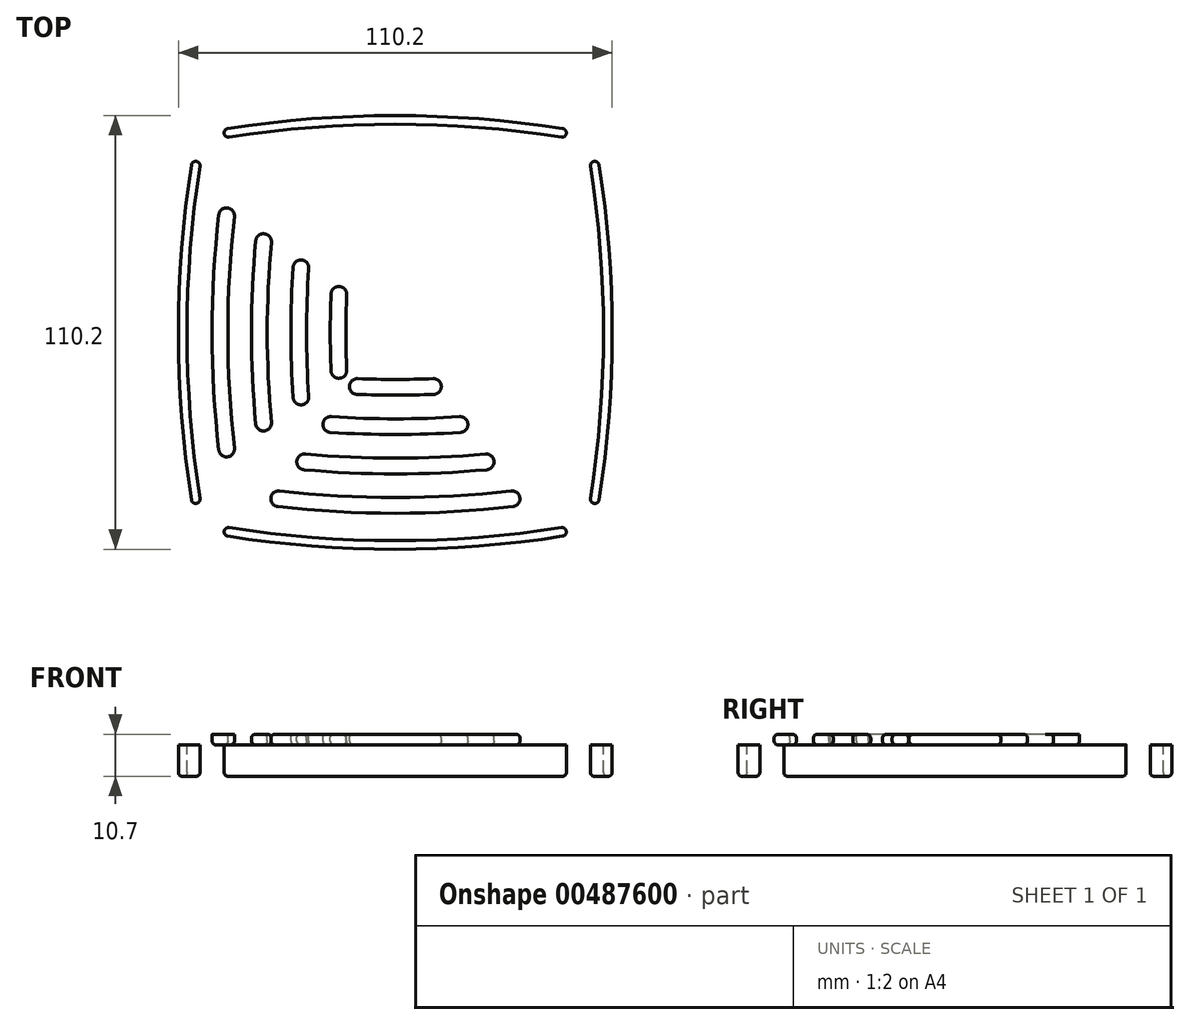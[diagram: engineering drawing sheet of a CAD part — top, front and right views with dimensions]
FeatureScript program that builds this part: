
annotation { "Feature Type Name" : "Feature", "Feature Type Description" : "" }
export const myFeature = defineFeature(function(context is Context, id is Id, definition is map)
    precondition{}
    {
        {
            var Q0;
            Q0=qCreatedBy(makeId("Top.planeOp"),FACE);
            var sketch = newSketch(context, id + "F0", { "sketchPlane" : qUnion([Q0])});
            skArc(sketch, "E0", {"start": v(58, 58) * mm, "mid": v(0, 64) * mm, "end": v(-58, 58) * mm});
            skPoint(sketch, "E1", {"position": v(0, 64) * mm});
            skArc(sketch, "E2.MirrorCS", {"start": v(58, -58) * mm, "mid": v(0, -64) * mm, "end": v(-58, -58) * mm});
            skArc(sketch, "E3", {"start": v(-58, 58) * mm, "mid": v(-64, 0) * mm, "end": v(-58, -58) * mm});
            skArc(sketch, "E4.MirrorCS", {"start": v(58, 58) * mm, "mid": v(64, 0) * mm, "end": v(58, -58) * mm});
            skSolve(sketch);
        }
        {
            var Q0;
            Q0=makeQuery(id+"F0.imprint","IMPRINT",FACE,{"disambiguationData":[TD([[makeQuery(id+"F0.imprint","IMPRINT",EDGE,{"derivedFrom":sQuery(id+"F0.wireOp",EDGE,"E0")}),1.0]])]});
            extrude(context, id + "F1", {"entities" : qUnion([Q0]), "depth" : 2.7 * mm});
        }
        {
            var Q0;
            Q0=makeQuery(id+"F1.opExtrude","SWEPT_EDGE",EDGE,{"disambiguationData":[OSD([sQuery(id+"F0.wireOp",EDGE,"E0"),sQuery(id+"F0.wireOp",EDGE,"E3")])]});
            var Q1;
            Q1=makeQuery(id+"F1.opExtrude","SWEPT_EDGE",EDGE,{"disambiguationData":[OSD([sQuery(id+"F0.wireOp",EDGE,"E2.MirrorCS"),sQuery(id+"F0.wireOp",EDGE,"E3")])]});
            var Q2;
            Q2=makeQuery(id+"F1.opExtrude","SWEPT_EDGE",EDGE,{"disambiguationData":[OSD([sQuery(id+"F0.wireOp",EDGE,"E0"),sQuery(id+"F0.wireOp",EDGE,"E4.MirrorCS")])]});
            var Q3;
            Q3=makeQuery(id+"F1.opExtrude","SWEPT_EDGE",EDGE,{"disambiguationData":[OSD([sQuery(id+"F0.wireOp",EDGE,"E2.MirrorCS"),sQuery(id+"F0.wireOp",EDGE,"E4.MirrorCS")])]});
            fillet(context, id + "F2", {"entities" : qUnion([Q0, Q1, Q2, Q3]), "radius" : 20 * mm, "tangentPropagation" : true, "allowEdgeOverflow" : false});
        }
        {
            var Q0;
            Q0=makeQuery(id+"F1.opExtrude","CAP_FACE",FACE,{"disambiguationData":[OSD([sQuery(id+"F0.wireOp",EDGE,"E0"),sQuery(id+"F0.wireOp",EDGE,"E2.MirrorCS"),sQuery(id+"F0.wireOp",EDGE,"E3"),sQuery(id+"F0.wireOp",EDGE,"E4.MirrorCS")])],"isStart":false});
            var sketch = newSketch(context, id + "F3", { "sketchPlane" : qUnion([Q0])});
            skArc(sketch, "E5.0", {"start": v(-42.84, 29.64) * mm, "mid": v(-44.52, 0) * mm, "end": v(-42.84, -29.64) * mm});
            skArc(sketch, "E6.0", {"start": v(-33.47, 23.07) * mm, "mid": v(-34.52, 0) * mm, "end": v(-33.47, -23.07) * mm});
            skArc(sketch, "E7.0", {"start": v(-23.96, 16.42) * mm, "mid": v(-24.52, 0) * mm, "end": v(-23.96, -16.42) * mm});
            skArc(sketch, "E8.0", {"start": v(-14.32, 9.66) * mm, "mid": v(-14.52, 0) * mm, "end": v(-14.32, -9.66) * mm});
            skArc(sketch, "E9.0.startCap", {"start": v(-44.83, 29.86) * mm, "mid": v(-42.62, 31.62) * mm, "end": v(-40.86, 29.41) * mm});
            skArc(sketch, "E9.0.endCap", {"start": v(-40.86, -29.41) * mm, "mid": v(-42.62, -31.62) * mm, "end": v(-44.83, -29.86) * mm});
            skArc(sketch, "E9.0.left", {"start": v(-40.86, 29.41) * mm, "mid": v(-42.52, 0) * mm, "end": v(-40.86, -29.41) * mm});
            skArc(sketch, "E9.0.right", {"start": v(-44.83, 29.86) * mm, "mid": v(-46.52, 0) * mm, "end": v(-44.83, -29.86) * mm});
            skArc(sketch, "E9.1.startCap", {"start": v(-35.46, 23.25) * mm, "mid": v(-33.28, 25.06) * mm, "end": v(-31.47, 22.89) * mm});
            skArc(sketch, "E9.1.endCap", {"start": v(-31.47, -22.89) * mm, "mid": v(-33.28, -25.06) * mm, "end": v(-35.46, -23.25) * mm});
            skArc(sketch, "E9.1.left", {"start": v(-31.47, 22.89) * mm, "mid": v(-32.52, 0) * mm, "end": v(-31.47, -22.89) * mm});
            skArc(sketch, "E9.1.right", {"start": v(-35.46, 23.25) * mm, "mid": v(-36.52, 0) * mm, "end": v(-35.46, -23.25) * mm});
            skArc(sketch, "E9.2.startCap", {"start": v(-25.96, 16.55) * mm, "mid": v(-23.83, 18.41) * mm, "end": v(-21.97, 16.28) * mm});
            skArc(sketch, "E9.2.endCap", {"start": v(-21.97, -16.28) * mm, "mid": v(-23.83, -18.41) * mm, "end": v(-25.96, -16.55) * mm});
            skArc(sketch, "E9.2.left", {"start": v(-21.97, 16.28) * mm, "mid": v(-22.52, 0) * mm, "end": v(-21.97, -16.28) * mm});
            skArc(sketch, "E9.2.right", {"start": v(-25.96, 16.55) * mm, "mid": v(-26.52, 0) * mm, "end": v(-25.96, -16.55) * mm});
            skArc(sketch, "E9.3.startCap", {"start": v(-16.32, 9.75) * mm, "mid": v(-14.24, 11.66) * mm, "end": v(-12.32, 9.58) * mm});
            skArc(sketch, "E9.3.endCap", {"start": v(-12.32, -9.58) * mm, "mid": v(-14.24, -11.66) * mm, "end": v(-16.32, -9.75) * mm});
            skArc(sketch, "E9.3.left", {"start": v(-12.32, 9.58) * mm, "mid": v(-12.52, 0) * mm, "end": v(-12.32, -9.58) * mm});
            skArc(sketch, "E9.3.right", {"start": v(-16.32, 9.75) * mm, "mid": v(-16.52, 0) * mm, "end": v(-16.32, -9.75) * mm});
            skArc(sketch, "E10.MirrorCS", {"start": v(20.93, -16.28) * mm, "mid": v(22.8, -18.41) * mm, "end": v(24.92, -16.55) * mm});
            skArc(sketch, "E11.MirrorCS", {"start": v(30.44, -22.89) * mm, "mid": v(32.25, -25.06) * mm, "end": v(34.42, -23.25) * mm});
            skArc(sketch, "E12.MirrorCS", {"start": v(15.28, 9.75) * mm, "mid": v(13.2, 11.66) * mm, "end": v(11.28, 9.58) * mm});
            skArc(sketch, "E13.MirrorCS", {"start": v(34.42, 23.25) * mm, "mid": v(32.25, 25.06) * mm, "end": v(30.44, 22.89) * mm});
            skArc(sketch, "E14.MirrorCS", {"start": v(39.82, -29.41) * mm, "mid": v(41.58, -31.62) * mm, "end": v(43.8, -29.86) * mm});
            skArc(sketch, "E15.MirrorCS", {"start": v(24.92, 16.55) * mm, "mid": v(22.8, 18.41) * mm, "end": v(20.93, 16.28) * mm});
            skArc(sketch, "E16.MirrorCS", {"start": v(11.28, -9.58) * mm, "mid": v(13.2, -11.66) * mm, "end": v(15.28, -9.75) * mm});
            skArc(sketch, "E17.MirrorCS", {"start": v(24.92, 16.55) * mm, "mid": v(25.48, 0) * mm, "end": v(24.92, -16.55) * mm});
            skArc(sketch, "E18.MirrorCS", {"start": v(11.28, 9.58) * mm, "mid": v(11.48, 0) * mm, "end": v(11.28, -9.58) * mm});
            skArc(sketch, "E19.MirrorCS", {"start": v(20.93, 16.28) * mm, "mid": v(21.48, 0) * mm, "end": v(20.93, -16.28) * mm});
            skArc(sketch, "E20.MirrorCS", {"start": v(41.8, 29.64) * mm, "mid": v(43.48, 0) * mm, "end": v(41.8, -29.64) * mm});
            skArc(sketch, "E21.MirrorCS", {"start": v(43.8, 29.86) * mm, "mid": v(45.48, 0) * mm, "end": v(43.8, -29.86) * mm});
            skArc(sketch, "E22.MirrorCS", {"start": v(34.42, 23.25) * mm, "mid": v(35.48, 0) * mm, "end": v(34.42, -23.25) * mm});
            skArc(sketch, "E23.MirrorCS", {"start": v(15.28, 9.75) * mm, "mid": v(15.48, 0) * mm, "end": v(15.28, -9.75) * mm});
            skArc(sketch, "E24.MirrorCS", {"start": v(32.43, 23.07) * mm, "mid": v(33.48, 0) * mm, "end": v(32.43, -23.07) * mm});
            skArc(sketch, "E25.MirrorCS", {"start": v(13.28, 9.66) * mm, "mid": v(13.48, 0) * mm, "end": v(13.28, -9.66) * mm});
            skArc(sketch, "E26.MirrorCS", {"start": v(43.8, 29.86) * mm, "mid": v(41.58, 31.62) * mm, "end": v(39.82, 29.41) * mm});
            skArc(sketch, "E27.MirrorCS", {"start": v(39.82, 29.41) * mm, "mid": v(41.48, 0) * mm, "end": v(39.82, -29.41) * mm});
            skArc(sketch, "E28.MirrorCS", {"start": v(22.93, 16.42) * mm, "mid": v(23.48, 0) * mm, "end": v(22.93, -16.42) * mm});
            skArc(sketch, "E29.MirrorCS", {"start": v(30.44, 22.89) * mm, "mid": v(31.48, 0) * mm, "end": v(30.44, -22.89) * mm});
            skArc(sketch, "E30.0", {"start": v(-29.6, -42.28) * mm, "mid": v(0.04, -43.96) * mm, "end": v(29.68, -42.28) * mm});
            skArc(sketch, "E31.0", {"start": v(-23.03, -32.9) * mm, "mid": v(0.04, -33.96) * mm, "end": v(23.11, -32.9) * mm});
            skArc(sketch, "E32.0", {"start": v(-16.37, -23.4) * mm, "mid": v(0.04, -23.96) * mm, "end": v(16.46, -23.4) * mm});
            skArc(sketch, "E33.0", {"start": v(-9.62, -13.76) * mm, "mid": v(0.04, -13.96) * mm, "end": v(9.7, -13.76) * mm});
            skArc(sketch, "E34.0.startCap", {"start": v(-29.82, -44.27) * mm, "mid": v(-31.58, -42.06) * mm, "end": v(-29.37, -40.3) * mm});
            skArc(sketch, "E34.0.endCap", {"start": v(29.46, -40.3) * mm, "mid": v(31.67, -42.06) * mm, "end": v(29.9, -44.27) * mm});
            skArc(sketch, "E34.0.left", {"start": v(-29.37, -40.3) * mm, "mid": v(0.04, -41.96) * mm, "end": v(29.46, -40.3) * mm});
            skArc(sketch, "E34.0.right", {"start": v(-29.82, -44.27) * mm, "mid": v(0.04, -45.96) * mm, "end": v(29.9, -44.27) * mm});
            skArc(sketch, "E34.1.startCap", {"start": v(-23.2, -34.9) * mm, "mid": v(-25.02, -32.72) * mm, "end": v(-22.84, -30.91) * mm});
            skArc(sketch, "E34.1.endCap", {"start": v(22.93, -30.91) * mm, "mid": v(25.1, -32.72) * mm, "end": v(23.3, -34.9) * mm});
            skArc(sketch, "E34.1.left", {"start": v(-22.84, -30.91) * mm, "mid": v(0.04, -31.96) * mm, "end": v(22.93, -30.91) * mm});
            skArc(sketch, "E34.1.right", {"start": v(-23.2, -34.9) * mm, "mid": v(0.04, -35.96) * mm, "end": v(23.3, -34.9) * mm});
            skArc(sketch, "E34.2.startCap", {"start": v(-16.5, -25.4) * mm, "mid": v(-18.37, -23.27) * mm, "end": v(-16.24, -21.4) * mm});
            skArc(sketch, "E34.2.endCap", {"start": v(16.32, -21.4) * mm, "mid": v(18.46, -23.27) * mm, "end": v(16.6, -25.4) * mm});
            skArc(sketch, "E34.2.left", {"start": v(-16.24, -21.4) * mm, "mid": v(0.04, -21.96) * mm, "end": v(16.32, -21.4) * mm});
            skArc(sketch, "E34.2.right", {"start": v(-16.5, -25.4) * mm, "mid": v(0.04, -25.96) * mm, "end": v(16.6, -25.4) * mm});
            skArc(sketch, "E34.3.startCap", {"start": v(-9.7, -15.75) * mm, "mid": v(-11.62, -13.67) * mm, "end": v(-9.54, -11.76) * mm});
            skArc(sketch, "E34.3.endCap", {"start": v(9.62, -11.76) * mm, "mid": v(11.7, -13.67) * mm, "end": v(9.79, -15.75) * mm});
            skArc(sketch, "E34.3.left", {"start": v(-9.54, -11.76) * mm, "mid": v(0.04, -11.96) * mm, "end": v(9.62, -11.76) * mm});
            skArc(sketch, "E34.3.right", {"start": v(-9.7, -15.75) * mm, "mid": v(0.04, -15.96) * mm, "end": v(9.79, -15.75) * mm});
            skArc(sketch, "E35.MirrorCS", {"start": v(16.32, 21.5) * mm, "mid": v(18.46, 23.36) * mm, "end": v(16.6, 25.49) * mm});
            skArc(sketch, "E36.MirrorCS", {"start": v(22.93, 31) * mm, "mid": v(25.1, 32.8) * mm, "end": v(23.3, 34.98) * mm});
            skArc(sketch, "E37.MirrorCS", {"start": v(-9.7, 15.84) * mm, "mid": v(-11.62, 13.76) * mm, "end": v(-9.54, 11.85) * mm});
            skArc(sketch, "E38.MirrorCS", {"start": v(-23.2, 34.98) * mm, "mid": v(-25.02, 32.8) * mm, "end": v(-22.84, 31) * mm});
            skArc(sketch, "E39.MirrorCS", {"start": v(29.46, 40.38) * mm, "mid": v(31.67, 42.15) * mm, "end": v(29.9, 44.36) * mm});
            skArc(sketch, "E40.MirrorCS", {"start": v(-16.5, 25.49) * mm, "mid": v(-18.37, 23.36) * mm, "end": v(-16.24, 21.5) * mm});
            skArc(sketch, "E41.MirrorCS", {"start": v(9.62, 11.85) * mm, "mid": v(11.7, 13.76) * mm, "end": v(9.79, 15.84) * mm});
            skArc(sketch, "E42.MirrorCS", {"start": v(-16.5, 25.49) * mm, "mid": v(0.04, 26.04) * mm, "end": v(16.6, 25.49) * mm});
            skArc(sketch, "E43.MirrorCS", {"start": v(-9.54, 11.85) * mm, "mid": v(0.04, 12.04) * mm, "end": v(9.62, 11.85) * mm});
            skArc(sketch, "E44.MirrorCS", {"start": v(-16.24, 21.5) * mm, "mid": v(0.04, 22.04) * mm, "end": v(16.32, 21.5) * mm});
            skArc(sketch, "E45.MirrorCS", {"start": v(-29.6, 42.37) * mm, "mid": v(0.04, 44.04) * mm, "end": v(29.68, 42.37) * mm});
            skArc(sketch, "E46.MirrorCS", {"start": v(-29.82, 44.36) * mm, "mid": v(0.04, 46.04) * mm, "end": v(29.9, 44.36) * mm});
            skArc(sketch, "E47.MirrorCS", {"start": v(-23.2, 34.98) * mm, "mid": v(0.04, 36.04) * mm, "end": v(23.3, 34.98) * mm});
            skArc(sketch, "E48.MirrorCS", {"start": v(-9.7, 15.84) * mm, "mid": v(0.04, 16.04) * mm, "end": v(9.79, 15.84) * mm});
            skArc(sketch, "E49.MirrorCS", {"start": v(-23.03, 33) * mm, "mid": v(0.04, 34.04) * mm, "end": v(23.11, 33) * mm});
            skArc(sketch, "E50.MirrorCS", {"start": v(-9.62, 13.84) * mm, "mid": v(0.04, 14.04) * mm, "end": v(9.7, 13.84) * mm});
            skArc(sketch, "E51.MirrorCS", {"start": v(-29.82, 44.36) * mm, "mid": v(-31.58, 42.15) * mm, "end": v(-29.37, 40.38) * mm});
            skArc(sketch, "E52.MirrorCS", {"start": v(-29.37, 40.38) * mm, "mid": v(0.04, 42.04) * mm, "end": v(29.46, 40.38) * mm});
            skArc(sketch, "E53.MirrorCS", {"start": v(-16.37, 23.5) * mm, "mid": v(0.04, 24.04) * mm, "end": v(16.46, 23.5) * mm});
            skArc(sketch, "E54.MirrorCS", {"start": v(-22.84, 31) * mm, "mid": v(0.04, 32.04) * mm, "end": v(22.93, 31) * mm});
            skSolve(sketch);
        }
        {
            var Q0;
            Q0=makeQuery(id+"F3.imprint","IMPRINT",FACE,{"disambiguationData":[TD([[makeQuery(id+"F3.imprint","IMPRINT",EDGE,{"derivedFrom":sQuery(id+"F3.wireOp",EDGE,"E9.0.startCap")}),-1.0]])]});
            var Q1;
            Q1=makeQuery(id+"F3.imprint","IMPRINT",FACE,{"disambiguationData":[TD([[makeQuery(id+"F3.imprint","IMPRINT",EDGE,{"derivedFrom":sQuery(id+"F3.wireOp",EDGE,"E9.1.startCap")}),-1.0]])]});
            var Q2;
            Q2=makeQuery(id+"F3.imprint","IMPRINT",FACE,{"disambiguationData":[TD([[makeQuery(id+"F3.imprint","IMPRINT",EDGE,{"derivedFrom":sQuery(id+"F3.wireOp",EDGE,"E9.2.startCap")}),-1.0]])]});
            var Q3;
            Q3=makeQuery(id+"F3.imprint","IMPRINT",FACE,{"disambiguationData":[TD([[makeQuery(id+"F3.imprint","IMPRINT",EDGE,{"derivedFrom":sQuery(id+"F3.wireOp",EDGE,"E9.3.startCap")}),-1.0]])]});
            var Q4;
            Q4=makeQuery(id+"F3.imprint","IMPRINT",FACE,{"disambiguationData":[TD([[makeQuery(id+"F3.imprint","IMPRINT",EDGE,{"derivedFrom":sQuery(id+"F3.wireOp",EDGE,"E10.MirrorCS")}),1.0]])]});
            var Q5;
            Q5=makeQuery(id+"F3.imprint","IMPRINT",FACE,{"disambiguationData":[TD([[makeQuery(id+"F3.imprint","IMPRINT",EDGE,{"derivedFrom":sQuery(id+"F3.wireOp",EDGE,"E11.MirrorCS")}),1.0]])]});
            var Q6;
            Q6=makeQuery(id+"F3.imprint","IMPRINT",FACE,{"disambiguationData":[TD([[makeQuery(id+"F3.imprint","IMPRINT",EDGE,{"derivedFrom":sQuery(id+"F3.wireOp",EDGE,"E12.MirrorCS")}),1.0]])]});
            var Q7;
            Q7=makeQuery(id+"F3.imprint","IMPRINT",FACE,{"disambiguationData":[TD([[makeQuery(id+"F3.imprint","IMPRINT",EDGE,{"derivedFrom":sQuery(id+"F3.wireOp",EDGE,"E14.MirrorCS")}),1.0]])]});
            var Q8;
            Q8=makeQuery(id+"F3.imprint","IMPRINT",FACE,{"disambiguationData":[TD([[makeQuery(id+"F3.imprint","IMPRINT",EDGE,{"derivedFrom":sQuery(id+"F3.wireOp",EDGE,"E34.0.startCap")}),-1.0]])]});
            var Q9;
            Q9=makeQuery(id+"F3.imprint","IMPRINT",FACE,{"disambiguationData":[TD([[makeQuery(id+"F3.imprint","IMPRINT",EDGE,{"derivedFrom":sQuery(id+"F3.wireOp",EDGE,"E34.2.startCap")}),-1.0]])]});
            var Q10;
            Q10=makeQuery(id+"F3.imprint","IMPRINT",FACE,{"disambiguationData":[TD([[makeQuery(id+"F3.imprint","IMPRINT",EDGE,{"derivedFrom":sQuery(id+"F3.wireOp",EDGE,"E35.MirrorCS")}),1.0]])]});
            var Q11;
            Q11=makeQuery(id+"F3.imprint","IMPRINT",FACE,{"disambiguationData":[TD([[makeQuery(id+"F3.imprint","IMPRINT",EDGE,{"derivedFrom":sQuery(id+"F3.wireOp",EDGE,"E34.3.startCap")}),-1.0]])]});
            var Q12;
            Q12=makeQuery(id+"F3.imprint","IMPRINT",FACE,{"disambiguationData":[TD([[makeQuery(id+"F3.imprint","IMPRINT",EDGE,{"derivedFrom":sQuery(id+"F3.wireOp",EDGE,"E37.MirrorCS")}),1.0]])]});
            var Q13;
            Q13=makeQuery(id+"F3.imprint","IMPRINT",FACE,{"disambiguationData":[TD([[makeQuery(id+"F3.imprint","IMPRINT",EDGE,{"derivedFrom":sQuery(id+"F3.wireOp",EDGE,"E36.MirrorCS")}),1.0]])]});
            var Q14;
            Q14=makeQuery(id+"F3.imprint","IMPRINT",FACE,{"disambiguationData":[TD([[makeQuery(id+"F3.imprint","IMPRINT",EDGE,{"derivedFrom":sQuery(id+"F3.wireOp",EDGE,"E34.1.startCap")}),-1.0]])]});
            var Q15;
            Q15=makeQuery(id+"F3.imprint","IMPRINT",FACE,{"disambiguationData":[TD([[makeQuery(id+"F3.imprint","IMPRINT",EDGE,{"derivedFrom":sQuery(id+"F3.wireOp",EDGE,"E39.MirrorCS")}),1.0]])]});
            extrude(context, id + "F4", {"entities" : qUnion([Q0, Q1, Q2, Q3, Q4, Q5, Q6, Q7, Q8, Q9, Q10, Q11, Q12, Q13, Q14, Q15]), "operationType" : NewBodyOperationType.REMOVE, "endBound" : BoundingType.THROUGH_ALL, "oppositeDirection" : true, "depth" : 25 * mm});
        }
        {
            var Q0;
            Q0=makeQuery(id+"F1.opExtrude","CAP_FACE",FACE,{"disambiguationData":[OSD([sQuery(id+"F0.wireOp",EDGE,"E0"),sQuery(id+"F0.wireOp",EDGE,"E2.MirrorCS"),sQuery(id+"F0.wireOp",EDGE,"E3"),sQuery(id+"F0.wireOp",EDGE,"E4.MirrorCS")])],"isStart":false});
            var sketch = newSketch(context, id + "F5", { "sketchPlane" : qUnion([Q0])});
            skCircle(sketch, "E55", {"center": v(0, 0) * mm, "radius": 5 * mm});
            skSolve(sketch);
        }
        {
            var Q0;
            Q0 = qSketchRegion(id + "F5", true);
            extrude(context, id + "F6", {"entities" : qUnion([Q0]), "operationType" : NewBodyOperationType.REMOVE, "endBound" : BoundingType.THROUGH_ALL, "oppositeDirection" : true, "depth" : 25 * mm});
        }
        {
            var Q0;
            Q0=makeQuery(id+"F1.opExtrude","CAP_FACE",FACE,{"disambiguationData":[OSD([sQuery(id+"F0.wireOp",EDGE,"E0"),sQuery(id+"F0.wireOp",EDGE,"E2.MirrorCS"),sQuery(id+"F0.wireOp",EDGE,"E3"),sQuery(id+"F0.wireOp",EDGE,"E4.MirrorCS")])],"isStart":true});
            var sketch = newSketch(context, id + "F7", { "sketchPlane" : qUnion([Q0])});
            skArc(sketch, "E56.0", {"start": v(-50.7, -42.37) * mm, "mid": v(-54, 0) * mm, "end": v(-50.7, 42.37) * mm});
            skArc(sketch, "E57.MirrorCS", {"start": v(50.7, -42.37) * mm, "mid": v(54, 0) * mm, "end": v(50.7, 42.37) * mm});
            skArc(sketch, "E58.0", {"start": v(42.37, 50.7) * mm, "mid": v(0, 54) * mm, "end": v(-42.37, 50.7) * mm});
            skArc(sketch, "E59.MirrorCS", {"start": v(42.37, -50.7) * mm, "mid": v(0, -54) * mm, "end": v(-42.37, -50.7) * mm});
            skArc(sketch, "E60.0.startCap", {"start": v(-49.6, -42.2) * mm, "mid": v(-50.53, -43.45) * mm, "end": v(-51.78, -42.54) * mm});
            skArc(sketch, "E60.0.endCap", {"start": v(-51.78, 42.54) * mm, "mid": v(-50.53, 43.45) * mm, "end": v(-49.6, 42.2) * mm});
            skArc(sketch, "E60.0.left", {"start": v(-51.78, -42.54) * mm, "mid": v(-55.1, 0) * mm, "end": v(-51.78, 42.54) * mm});
            skArc(sketch, "E60.0.right", {"start": v(-49.6, -42.2) * mm, "mid": v(-52.9, 0) * mm, "end": v(-49.6, 42.2) * mm});
            skArc(sketch, "E60.1.startCap", {"start": v(42.54, 51.78) * mm, "mid": v(43.45, 50.53) * mm, "end": v(42.2, 49.6) * mm});
            skArc(sketch, "E60.1.endCap", {"start": v(-42.2, 49.6) * mm, "mid": v(-43.45, 50.53) * mm, "end": v(-42.54, 51.78) * mm});
            skArc(sketch, "E60.1.left", {"start": v(42.2, 49.6) * mm, "mid": v(0, 52.9) * mm, "end": v(-42.2, 49.6) * mm});
            skArc(sketch, "E60.1.right", {"start": v(42.54, 51.78) * mm, "mid": v(0, 55.1) * mm, "end": v(-42.54, 51.78) * mm});
            skArc(sketch, "E60.2.startCap", {"start": v(51.78, -42.54) * mm, "mid": v(50.53, -43.45) * mm, "end": v(49.6, -42.2) * mm});
            skArc(sketch, "E60.2.endCap", {"start": v(49.6, 42.2) * mm, "mid": v(50.53, 43.45) * mm, "end": v(51.78, 42.54) * mm});
            skArc(sketch, "E60.2.left", {"start": v(49.6, -42.2) * mm, "mid": v(52.9, 0) * mm, "end": v(49.6, 42.2) * mm});
            skArc(sketch, "E60.2.right", {"start": v(51.78, -42.54) * mm, "mid": v(55.1, 0) * mm, "end": v(51.78, 42.54) * mm});
            skArc(sketch, "E60.3.startCap", {"start": v(42.2, -49.6) * mm, "mid": v(43.45, -50.53) * mm, "end": v(42.54, -51.78) * mm});
            skArc(sketch, "E60.3.endCap", {"start": v(-42.54, -51.78) * mm, "mid": v(-43.45, -50.53) * mm, "end": v(-42.2, -49.6) * mm});
            skArc(sketch, "E60.3.left", {"start": v(42.54, -51.78) * mm, "mid": v(0, -55.1) * mm, "end": v(-42.54, -51.78) * mm});
            skArc(sketch, "E60.3.right", {"start": v(42.2, -49.6) * mm, "mid": v(0, -52.9) * mm, "end": v(-42.2, -49.6) * mm});
            skSolve(sketch);
        }
        {
            var Q0;
            Q0 = qSketchRegion(id + "F7", true);
            extrude(context, id + "F8", {"entities" : qUnion([Q0]), "operationType" : NewBodyOperationType.ADD, "depth" : 8 * mm});
        }
        {
            var Q0;
            Q0=makeQuery(id+"F1.opExtrude","CAP_EDGE",EDGE,{"disambiguationData":[OSD([sQuery(id+"F0.wireOp",EDGE,"E3")])],"isStart":false});
            var Q1;
            {var subQ0=sQuery(id+"F0.wireOp",EDGE,"E3");var subQ1=sQuery(id+"F0.wireOp",EDGE,"E0");Q1=makeQuery(id+"F2.opFillet","BLEND_EDGE",EDGE,{"blendedFrom":[makeQuery(id+"F1.opExtrude","SWEPT_EDGE",EDGE,{"disambiguationData":[OSD([subQ1,subQ0])]}),makeQuery(id+"F1.opExtrude","CAP_FACE",FACE,{"disambiguationData":[OSD([subQ1,sQuery(id+"F0.wireOp",EDGE,"E2.MirrorCS"),subQ0,sQuery(id+"F0.wireOp",EDGE,"E4.MirrorCS")])],"isStart":false})],"blendedInto":[makeQuery(id+"F1.opExtrude","CAP_FACE",FACE,{"disambiguationData":[OSD([subQ1,sQuery(id+"F0.wireOp",EDGE,"E2.MirrorCS"),subQ0,sQuery(id+"F0.wireOp",EDGE,"E4.MirrorCS")])],"isStart":false})]});}
            var Q2;
            Q2=makeQuery(id+"F1.opExtrude","CAP_EDGE",EDGE,{"disambiguationData":[OSD([sQuery(id+"F0.wireOp",EDGE,"E0")])],"isStart":false});
            var Q3;
            {var subQ0=sQuery(id+"F0.wireOp",EDGE,"E3");var subQ1=sQuery(id+"F0.wireOp",EDGE,"E2.MirrorCS");Q3=makeQuery(id+"F2.opFillet","BLEND_EDGE",EDGE,{"blendedFrom":[makeQuery(id+"F1.opExtrude","SWEPT_EDGE",EDGE,{"disambiguationData":[OSD([subQ1,subQ0])]}),makeQuery(id+"F1.opExtrude","CAP_FACE",FACE,{"disambiguationData":[OSD([sQuery(id+"F0.wireOp",EDGE,"E0"),subQ1,subQ0,sQuery(id+"F0.wireOp",EDGE,"E4.MirrorCS")])],"isStart":false})],"blendedInto":[makeQuery(id+"F1.opExtrude","CAP_FACE",FACE,{"disambiguationData":[OSD([sQuery(id+"F0.wireOp",EDGE,"E0"),subQ1,subQ0,sQuery(id+"F0.wireOp",EDGE,"E4.MirrorCS")])],"isStart":false})]});}
            var Q4;
            Q4=makeQuery(id+"F1.opExtrude","CAP_EDGE",EDGE,{"disambiguationData":[OSD([sQuery(id+"F0.wireOp",EDGE,"E2.MirrorCS")])],"isStart":false});
            var Q5;
            {var subQ0=sQuery(id+"F0.wireOp",EDGE,"E4.MirrorCS");var subQ1=sQuery(id+"F0.wireOp",EDGE,"E2.MirrorCS");Q5=makeQuery(id+"F2.opFillet","BLEND_EDGE",EDGE,{"blendedFrom":[makeQuery(id+"F1.opExtrude","SWEPT_EDGE",EDGE,{"disambiguationData":[OSD([subQ1,subQ0])]}),makeQuery(id+"F1.opExtrude","CAP_FACE",FACE,{"disambiguationData":[OSD([sQuery(id+"F0.wireOp",EDGE,"E0"),subQ1,sQuery(id+"F0.wireOp",EDGE,"E3"),subQ0])],"isStart":false})],"blendedInto":[makeQuery(id+"F1.opExtrude","CAP_FACE",FACE,{"disambiguationData":[OSD([sQuery(id+"F0.wireOp",EDGE,"E0"),subQ1,sQuery(id+"F0.wireOp",EDGE,"E3"),subQ0])],"isStart":false})]});}
            var Q6;
            Q6=makeQuery(id+"F1.opExtrude","CAP_EDGE",EDGE,{"disambiguationData":[OSD([sQuery(id+"F0.wireOp",EDGE,"E4.MirrorCS")])],"isStart":false});
            var Q7;
            Q7=makeQuery(id+"F1.opExtrude","CAP_EDGE",EDGE,{"disambiguationData":[OSD([sQuery(id+"F0.wireOp",EDGE,"E3")])],"isStart":true});
            var Q8;
            {var subQ0=sQuery(id+"F0.wireOp",EDGE,"E3");var subQ1=sQuery(id+"F0.wireOp",EDGE,"E2.MirrorCS");Q8=makeQuery(id+"F2.opFillet","BLEND_EDGE",EDGE,{"blendedFrom":[makeQuery(id+"F1.opExtrude","SWEPT_EDGE",EDGE,{"disambiguationData":[OSD([subQ1,subQ0])]}),makeQuery(id+"F1.opExtrude","CAP_FACE",FACE,{"disambiguationData":[OSD([sQuery(id+"F0.wireOp",EDGE,"E0"),subQ1,subQ0,sQuery(id+"F0.wireOp",EDGE,"E4.MirrorCS")])],"isStart":true})],"blendedInto":[makeQuery(id+"F1.opExtrude","CAP_FACE",FACE,{"disambiguationData":[OSD([sQuery(id+"F0.wireOp",EDGE,"E0"),subQ1,subQ0,sQuery(id+"F0.wireOp",EDGE,"E4.MirrorCS")])],"isStart":true})]});}
            var Q9;
            Q9=makeQuery(id+"F1.opExtrude","CAP_EDGE",EDGE,{"disambiguationData":[OSD([sQuery(id+"F0.wireOp",EDGE,"E2.MirrorCS")])],"isStart":true});
            var Q10;
            {var subQ0=sQuery(id+"F0.wireOp",EDGE,"E3");var subQ1=sQuery(id+"F0.wireOp",EDGE,"E0");Q10=makeQuery(id+"F2.opFillet","BLEND_EDGE",EDGE,{"blendedFrom":[makeQuery(id+"F1.opExtrude","SWEPT_EDGE",EDGE,{"disambiguationData":[OSD([subQ1,subQ0])]}),makeQuery(id+"F1.opExtrude","CAP_FACE",FACE,{"disambiguationData":[OSD([subQ1,sQuery(id+"F0.wireOp",EDGE,"E2.MirrorCS"),subQ0,sQuery(id+"F0.wireOp",EDGE,"E4.MirrorCS")])],"isStart":true})],"blendedInto":[makeQuery(id+"F1.opExtrude","CAP_FACE",FACE,{"disambiguationData":[OSD([subQ1,sQuery(id+"F0.wireOp",EDGE,"E2.MirrorCS"),subQ0,sQuery(id+"F0.wireOp",EDGE,"E4.MirrorCS")])],"isStart":true})]});}
            var Q11;
            Q11=makeQuery(id+"F1.opExtrude","CAP_EDGE",EDGE,{"disambiguationData":[OSD([sQuery(id+"F0.wireOp",EDGE,"E0")])],"isStart":true});
            var Q12;
            {var subQ0=sQuery(id+"F0.wireOp",EDGE,"E4.MirrorCS");var subQ1=sQuery(id+"F0.wireOp",EDGE,"E0");Q12=makeQuery(id+"F2.opFillet","BLEND_EDGE",EDGE,{"blendedFrom":[makeQuery(id+"F1.opExtrude","SWEPT_EDGE",EDGE,{"disambiguationData":[OSD([subQ1,subQ0])]}),makeQuery(id+"F1.opExtrude","CAP_FACE",FACE,{"disambiguationData":[OSD([subQ1,sQuery(id+"F0.wireOp",EDGE,"E2.MirrorCS"),sQuery(id+"F0.wireOp",EDGE,"E3"),subQ0])],"isStart":true})],"blendedInto":[makeQuery(id+"F1.opExtrude","CAP_FACE",FACE,{"disambiguationData":[OSD([subQ1,sQuery(id+"F0.wireOp",EDGE,"E2.MirrorCS"),sQuery(id+"F0.wireOp",EDGE,"E3"),subQ0])],"isStart":true})]});}
            var Q13;
            Q13=makeQuery(id+"F1.opExtrude","CAP_EDGE",EDGE,{"disambiguationData":[OSD([sQuery(id+"F0.wireOp",EDGE,"E4.MirrorCS")])],"isStart":true});
            var Q14;
            Q14=makeQuery(id+"F8.opExtrude","CAP_EDGE",EDGE,{"disambiguationData":[OSD([sQuery(id+"F7.wireOp",EDGE,"E60.1.right")])],"isStart":false});
            var Q15;
            Q15=makeQuery(id+"F8.opExtrude","CAP_EDGE",EDGE,{"disambiguationData":[OSD([sQuery(id+"F7.wireOp",EDGE,"E60.1.left")])],"isStart":false});
            var Q16;
            Q16=makeQuery(id+"F8.opExtrude","CAP_EDGE",EDGE,{"disambiguationData":[OSD([sQuery(id+"F7.wireOp",EDGE,"E60.2.right")])],"isStart":false});
            var Q17;
            Q17=makeQuery(id+"F8.opExtrude","CAP_EDGE",EDGE,{"disambiguationData":[OSD([sQuery(id+"F7.wireOp",EDGE,"E60.2.left")])],"isStart":false});
            var Q18;
            Q18=makeQuery(id+"F8.opExtrude","CAP_EDGE",EDGE,{"disambiguationData":[OSD([sQuery(id+"F7.wireOp",EDGE,"E60.3.right")])],"isStart":false});
            var Q19;
            Q19=makeQuery(id+"F8.opExtrude","CAP_EDGE",EDGE,{"disambiguationData":[OSD([sQuery(id+"F7.wireOp",EDGE,"E60.3.left")])],"isStart":false});
            var Q20;
            Q20=makeQuery(id+"F4.boolean.opBoolean","INTERSECT",EDGE,{"derivedFrom":[makeQuery(id+"F1.opExtrude","CAP_FACE",FACE,{"disambiguationData":[OSD([sQuery(id+"F0.wireOp",EDGE,"E0"),sQuery(id+"F0.wireOp",EDGE,"E2.MirrorCS"),sQuery(id+"F0.wireOp",EDGE,"E3"),sQuery(id+"F0.wireOp",EDGE,"E4.MirrorCS")])],"isStart":true}),makeQuery(id+"F4.opExtrude","SWEPT_FACE",FACE,{"disambiguationData":[OSD([sQuery(id+"F3.wireOp",EDGE,"E46.MirrorCS")])]})]});
            var Q21;
            Q21=makeQuery(id+"F4.boolean.opBoolean","INTERSECT",EDGE,{"derivedFrom":[makeQuery(id+"F1.opExtrude","CAP_FACE",FACE,{"disambiguationData":[OSD([sQuery(id+"F0.wireOp",EDGE,"E0"),sQuery(id+"F0.wireOp",EDGE,"E2.MirrorCS"),sQuery(id+"F0.wireOp",EDGE,"E3"),sQuery(id+"F0.wireOp",EDGE,"E4.MirrorCS")])],"isStart":true}),makeQuery(id+"F4.opExtrude","SWEPT_FACE",FACE,{"disambiguationData":[OSD([sQuery(id+"F3.wireOp",EDGE,"E52.MirrorCS")])]})]});
            var Q22;
            Q22=makeQuery(id+"F4.boolean.opBoolean","INTERSECT",EDGE,{"derivedFrom":[makeQuery(id+"F1.opExtrude","CAP_FACE",FACE,{"disambiguationData":[OSD([sQuery(id+"F0.wireOp",EDGE,"E0"),sQuery(id+"F0.wireOp",EDGE,"E2.MirrorCS"),sQuery(id+"F0.wireOp",EDGE,"E3"),sQuery(id+"F0.wireOp",EDGE,"E4.MirrorCS")])],"isStart":true}),makeQuery(id+"F4.opExtrude","SWEPT_FACE",FACE,{"disambiguationData":[OSD([sQuery(id+"F3.wireOp",EDGE,"E54.MirrorCS")])]})]});
            var Q23;
            Q23=makeQuery(id+"F4.boolean.opBoolean","INTERSECT",EDGE,{"derivedFrom":[makeQuery(id+"F1.opExtrude","CAP_FACE",FACE,{"disambiguationData":[OSD([sQuery(id+"F0.wireOp",EDGE,"E0"),sQuery(id+"F0.wireOp",EDGE,"E2.MirrorCS"),sQuery(id+"F0.wireOp",EDGE,"E3"),sQuery(id+"F0.wireOp",EDGE,"E4.MirrorCS")])],"isStart":true}),makeQuery(id+"F4.opExtrude","SWEPT_FACE",FACE,{"disambiguationData":[OSD([sQuery(id+"F3.wireOp",EDGE,"E47.MirrorCS")])]})]});
            var Q24;
            Q24=makeQuery(id+"F4.boolean.opBoolean","INTERSECT",EDGE,{"derivedFrom":[makeQuery(id+"F1.opExtrude","CAP_FACE",FACE,{"disambiguationData":[OSD([sQuery(id+"F0.wireOp",EDGE,"E0"),sQuery(id+"F0.wireOp",EDGE,"E2.MirrorCS"),sQuery(id+"F0.wireOp",EDGE,"E3"),sQuery(id+"F0.wireOp",EDGE,"E4.MirrorCS")])],"isStart":true}),makeQuery(id+"F4.opExtrude","SWEPT_FACE",FACE,{"disambiguationData":[OSD([sQuery(id+"F3.wireOp",EDGE,"E44.MirrorCS")])]})]});
            var Q25;
            Q25=makeQuery(id+"F4.boolean.opBoolean","INTERSECT",EDGE,{"derivedFrom":[makeQuery(id+"F1.opExtrude","CAP_FACE",FACE,{"disambiguationData":[OSD([sQuery(id+"F0.wireOp",EDGE,"E0"),sQuery(id+"F0.wireOp",EDGE,"E2.MirrorCS"),sQuery(id+"F0.wireOp",EDGE,"E3"),sQuery(id+"F0.wireOp",EDGE,"E4.MirrorCS")])],"isStart":true}),makeQuery(id+"F4.opExtrude","SWEPT_FACE",FACE,{"disambiguationData":[OSD([sQuery(id+"F3.wireOp",EDGE,"E42.MirrorCS")])]})]});
            var Q26;
            {var subQ0=sQuery(id+"F0.wireOp",EDGE,"E4.MirrorCS");var subQ1=sQuery(id+"F0.wireOp",EDGE,"E2.MirrorCS");Q26=makeQuery(id+"F2.opFillet","BLEND_EDGE",EDGE,{"blendedFrom":[makeQuery(id+"F1.opExtrude","SWEPT_EDGE",EDGE,{"disambiguationData":[OSD([subQ1,subQ0])]}),makeQuery(id+"F1.opExtrude","CAP_FACE",FACE,{"disambiguationData":[OSD([sQuery(id+"F0.wireOp",EDGE,"E0"),subQ1,sQuery(id+"F0.wireOp",EDGE,"E3"),subQ0])],"isStart":true})],"blendedInto":[makeQuery(id+"F1.opExtrude","CAP_FACE",FACE,{"disambiguationData":[OSD([sQuery(id+"F0.wireOp",EDGE,"E0"),subQ1,sQuery(id+"F0.wireOp",EDGE,"E3"),subQ0])],"isStart":true})]});}
            var Q27;
            Q27=makeQuery(id+"F4.boolean.opBoolean","INTERSECT",EDGE,{"derivedFrom":[makeQuery(id+"F1.opExtrude","CAP_FACE",FACE,{"disambiguationData":[OSD([sQuery(id+"F0.wireOp",EDGE,"E0"),sQuery(id+"F0.wireOp",EDGE,"E2.MirrorCS"),sQuery(id+"F0.wireOp",EDGE,"E3"),sQuery(id+"F0.wireOp",EDGE,"E4.MirrorCS")])],"isStart":true}),makeQuery(id+"F4.opExtrude","SWEPT_FACE",FACE,{"disambiguationData":[OSD([sQuery(id+"F3.wireOp",EDGE,"E43.MirrorCS")])]})]});
            var Q28;
            Q28=makeQuery(id+"F4.boolean.opBoolean","INTERSECT",EDGE,{"derivedFrom":[makeQuery(id+"F1.opExtrude","CAP_FACE",FACE,{"disambiguationData":[OSD([sQuery(id+"F0.wireOp",EDGE,"E0"),sQuery(id+"F0.wireOp",EDGE,"E2.MirrorCS"),sQuery(id+"F0.wireOp",EDGE,"E3"),sQuery(id+"F0.wireOp",EDGE,"E4.MirrorCS")])],"isStart":true}),makeQuery(id+"F4.opExtrude","SWEPT_FACE",FACE,{"disambiguationData":[OSD([sQuery(id+"F3.wireOp",EDGE,"E48.MirrorCS")])]})]});
            var Q29;
            Q29=makeQuery(id+"F4.boolean.opBoolean","INTERSECT",EDGE,{"derivedFrom":[makeQuery(id+"F1.opExtrude","CAP_FACE",FACE,{"disambiguationData":[OSD([sQuery(id+"F0.wireOp",EDGE,"E0"),sQuery(id+"F0.wireOp",EDGE,"E2.MirrorCS"),sQuery(id+"F0.wireOp",EDGE,"E3"),sQuery(id+"F0.wireOp",EDGE,"E4.MirrorCS")])],"isStart":true}),makeQuery(id+"F4.opExtrude","SWEPT_FACE",FACE,{"disambiguationData":[OSD([sQuery(id+"F3.wireOp",EDGE,"E29.MirrorCS")])]})]});
            var Q30;
            Q30=makeQuery(id+"F4.boolean.opBoolean","INTERSECT",EDGE,{"derivedFrom":[makeQuery(id+"F1.opExtrude","CAP_FACE",FACE,{"disambiguationData":[OSD([sQuery(id+"F0.wireOp",EDGE,"E0"),sQuery(id+"F0.wireOp",EDGE,"E2.MirrorCS"),sQuery(id+"F0.wireOp",EDGE,"E3"),sQuery(id+"F0.wireOp",EDGE,"E4.MirrorCS")])],"isStart":true}),makeQuery(id+"F4.opExtrude","SWEPT_FACE",FACE,{"disambiguationData":[OSD([sQuery(id+"F3.wireOp",EDGE,"E17.MirrorCS")])]})]});
            var Q31;
            Q31=makeQuery(id+"F4.boolean.opBoolean","INTERSECT",EDGE,{"derivedFrom":[makeQuery(id+"F1.opExtrude","CAP_FACE",FACE,{"disambiguationData":[OSD([sQuery(id+"F0.wireOp",EDGE,"E0"),sQuery(id+"F0.wireOp",EDGE,"E2.MirrorCS"),sQuery(id+"F0.wireOp",EDGE,"E3"),sQuery(id+"F0.wireOp",EDGE,"E4.MirrorCS")])],"isStart":true}),makeQuery(id+"F4.opExtrude","SWEPT_FACE",FACE,{"disambiguationData":[OSD([sQuery(id+"F3.wireOp",EDGE,"E19.MirrorCS")])]})]});
            var Q32;
            Q32=makeQuery(id+"F4.boolean.opBoolean","INTERSECT",EDGE,{"derivedFrom":[makeQuery(id+"F1.opExtrude","CAP_FACE",FACE,{"disambiguationData":[OSD([sQuery(id+"F0.wireOp",EDGE,"E0"),sQuery(id+"F0.wireOp",EDGE,"E2.MirrorCS"),sQuery(id+"F0.wireOp",EDGE,"E3"),sQuery(id+"F0.wireOp",EDGE,"E4.MirrorCS")])],"isStart":true}),makeQuery(id+"F4.opExtrude","SWEPT_FACE",FACE,{"disambiguationData":[OSD([sQuery(id+"F3.wireOp",EDGE,"E17.MirrorCS")])]})]});
            var Q33;
            Q33=makeQuery(id+"F4.boolean.opBoolean","INTERSECT",EDGE,{"derivedFrom":[makeQuery(id+"F1.opExtrude","CAP_FACE",FACE,{"disambiguationData":[OSD([sQuery(id+"F0.wireOp",EDGE,"E0"),sQuery(id+"F0.wireOp",EDGE,"E2.MirrorCS"),sQuery(id+"F0.wireOp",EDGE,"E3"),sQuery(id+"F0.wireOp",EDGE,"E4.MirrorCS")])],"isStart":true}),makeQuery(id+"F4.opExtrude","SWEPT_FACE",FACE,{"disambiguationData":[OSD([sQuery(id+"F3.wireOp",EDGE,"E23.MirrorCS")])]})]});
            var Q34;
            Q34=makeQuery(id+"F4.boolean.opBoolean","INTERSECT",EDGE,{"derivedFrom":[makeQuery(id+"F1.opExtrude","CAP_FACE",FACE,{"disambiguationData":[OSD([sQuery(id+"F0.wireOp",EDGE,"E0"),sQuery(id+"F0.wireOp",EDGE,"E2.MirrorCS"),sQuery(id+"F0.wireOp",EDGE,"E3"),sQuery(id+"F0.wireOp",EDGE,"E4.MirrorCS")])],"isStart":true}),makeQuery(id+"F4.opExtrude","SWEPT_FACE",FACE,{"disambiguationData":[OSD([sQuery(id+"F3.wireOp",EDGE,"E23.MirrorCS")])]})]});
            var Q35;
            Q35=makeQuery(id+"F4.boolean.opBoolean","INTERSECT",EDGE,{"derivedFrom":[makeQuery(id+"F1.opExtrude","CAP_FACE",FACE,{"disambiguationData":[OSD([sQuery(id+"F0.wireOp",EDGE,"E0"),sQuery(id+"F0.wireOp",EDGE,"E2.MirrorCS"),sQuery(id+"F0.wireOp",EDGE,"E3"),sQuery(id+"F0.wireOp",EDGE,"E4.MirrorCS")])],"isStart":true}),makeQuery(id+"F4.opExtrude","SWEPT_FACE",FACE,{"disambiguationData":[OSD([sQuery(id+"F3.wireOp",EDGE,"E18.MirrorCS")])]})]});
            var Q36;
            Q36=makeQuery(id+"F6.boolean.opBoolean","INTERSECT",EDGE,{"derivedFrom":[makeQuery(id+"F1.opExtrude","CAP_FACE",FACE,{"disambiguationData":[OSD([sQuery(id+"F0.wireOp",EDGE,"E0"),sQuery(id+"F0.wireOp",EDGE,"E2.MirrorCS"),sQuery(id+"F0.wireOp",EDGE,"E3"),sQuery(id+"F0.wireOp",EDGE,"E4.MirrorCS")])],"isStart":true}),makeQuery(id+"F6.opExtrude","SWEPT_FACE",FACE,{"disambiguationData":[OSD([sQuery(id+"F5.wireOp",EDGE,"E55")])]})]});
            var Q37;
            Q37=makeQuery(id+"F4.boolean.opBoolean","INTERSECT",EDGE,{"derivedFrom":[makeQuery(id+"F1.opExtrude","CAP_FACE",FACE,{"disambiguationData":[OSD([sQuery(id+"F0.wireOp",EDGE,"E0"),sQuery(id+"F0.wireOp",EDGE,"E2.MirrorCS"),sQuery(id+"F0.wireOp",EDGE,"E3"),sQuery(id+"F0.wireOp",EDGE,"E4.MirrorCS")])],"isStart":true}),makeQuery(id+"F4.opExtrude","SWEPT_FACE",FACE,{"disambiguationData":[OSD([sQuery(id+"F3.wireOp",EDGE,"E9.3.left")])]})]});
            var Q38;
            Q38=makeQuery(id+"F4.boolean.opBoolean","INTERSECT",EDGE,{"derivedFrom":[makeQuery(id+"F1.opExtrude","CAP_FACE",FACE,{"disambiguationData":[OSD([sQuery(id+"F0.wireOp",EDGE,"E0"),sQuery(id+"F0.wireOp",EDGE,"E2.MirrorCS"),sQuery(id+"F0.wireOp",EDGE,"E3"),sQuery(id+"F0.wireOp",EDGE,"E4.MirrorCS")])],"isStart":true}),makeQuery(id+"F4.opExtrude","SWEPT_FACE",FACE,{"disambiguationData":[OSD([sQuery(id+"F3.wireOp",EDGE,"E9.2.left")])]})]});
            var Q39;
            Q39=makeQuery(id+"F4.boolean.opBoolean","INTERSECT",EDGE,{"derivedFrom":[makeQuery(id+"F1.opExtrude","CAP_FACE",FACE,{"disambiguationData":[OSD([sQuery(id+"F0.wireOp",EDGE,"E0"),sQuery(id+"F0.wireOp",EDGE,"E2.MirrorCS"),sQuery(id+"F0.wireOp",EDGE,"E3"),sQuery(id+"F0.wireOp",EDGE,"E4.MirrorCS")])],"isStart":true}),makeQuery(id+"F4.opExtrude","SWEPT_FACE",FACE,{"disambiguationData":[OSD([sQuery(id+"F3.wireOp",EDGE,"E9.2.right")])]})]});
            var Q40;
            Q40=makeQuery(id+"F4.boolean.opBoolean","INTERSECT",EDGE,{"derivedFrom":[makeQuery(id+"F1.opExtrude","CAP_FACE",FACE,{"disambiguationData":[OSD([sQuery(id+"F0.wireOp",EDGE,"E0"),sQuery(id+"F0.wireOp",EDGE,"E2.MirrorCS"),sQuery(id+"F0.wireOp",EDGE,"E3"),sQuery(id+"F0.wireOp",EDGE,"E4.MirrorCS")])],"isStart":true}),makeQuery(id+"F4.opExtrude","SWEPT_FACE",FACE,{"disambiguationData":[OSD([sQuery(id+"F3.wireOp",EDGE,"E9.0.left")])]})]});
            var Q41;
            Q41=makeQuery(id+"F4.boolean.opBoolean","INTERSECT",EDGE,{"derivedFrom":[makeQuery(id+"F1.opExtrude","CAP_FACE",FACE,{"disambiguationData":[OSD([sQuery(id+"F0.wireOp",EDGE,"E0"),sQuery(id+"F0.wireOp",EDGE,"E2.MirrorCS"),sQuery(id+"F0.wireOp",EDGE,"E3"),sQuery(id+"F0.wireOp",EDGE,"E4.MirrorCS")])],"isStart":true}),makeQuery(id+"F4.opExtrude","SWEPT_FACE",FACE,{"disambiguationData":[OSD([sQuery(id+"F3.wireOp",EDGE,"E9.0.right")])]})]});
            var Q42;
            Q42=makeQuery(id+"F4.boolean.opBoolean","INTERSECT",EDGE,{"derivedFrom":[makeQuery(id+"F1.opExtrude","CAP_FACE",FACE,{"disambiguationData":[OSD([sQuery(id+"F0.wireOp",EDGE,"E0"),sQuery(id+"F0.wireOp",EDGE,"E2.MirrorCS"),sQuery(id+"F0.wireOp",EDGE,"E3"),sQuery(id+"F0.wireOp",EDGE,"E4.MirrorCS")])],"isStart":true}),makeQuery(id+"F4.opExtrude","SWEPT_FACE",FACE,{"disambiguationData":[OSD([sQuery(id+"F3.wireOp",EDGE,"E9.1.left")])]})]});
            var Q43;
            Q43=makeQuery(id+"F4.boolean.opBoolean","INTERSECT",EDGE,{"derivedFrom":[makeQuery(id+"F1.opExtrude","CAP_FACE",FACE,{"disambiguationData":[OSD([sQuery(id+"F0.wireOp",EDGE,"E0"),sQuery(id+"F0.wireOp",EDGE,"E2.MirrorCS"),sQuery(id+"F0.wireOp",EDGE,"E3"),sQuery(id+"F0.wireOp",EDGE,"E4.MirrorCS")])],"isStart":true}),makeQuery(id+"F4.opExtrude","SWEPT_FACE",FACE,{"disambiguationData":[OSD([sQuery(id+"F3.wireOp",EDGE,"E34.3.left")])]})]});
            var Q44;
            Q44=makeQuery(id+"F4.boolean.opBoolean","INTERSECT",EDGE,{"derivedFrom":[makeQuery(id+"F1.opExtrude","CAP_FACE",FACE,{"disambiguationData":[OSD([sQuery(id+"F0.wireOp",EDGE,"E0"),sQuery(id+"F0.wireOp",EDGE,"E2.MirrorCS"),sQuery(id+"F0.wireOp",EDGE,"E3"),sQuery(id+"F0.wireOp",EDGE,"E4.MirrorCS")])],"isStart":true}),makeQuery(id+"F4.opExtrude","SWEPT_FACE",FACE,{"disambiguationData":[OSD([sQuery(id+"F3.wireOp",EDGE,"E34.3.right")])]})]});
            var Q45;
            Q45=makeQuery(id+"F4.boolean.opBoolean","INTERSECT",EDGE,{"derivedFrom":[makeQuery(id+"F1.opExtrude","CAP_FACE",FACE,{"disambiguationData":[OSD([sQuery(id+"F0.wireOp",EDGE,"E0"),sQuery(id+"F0.wireOp",EDGE,"E2.MirrorCS"),sQuery(id+"F0.wireOp",EDGE,"E3"),sQuery(id+"F0.wireOp",EDGE,"E4.MirrorCS")])],"isStart":true}),makeQuery(id+"F4.opExtrude","SWEPT_FACE",FACE,{"disambiguationData":[OSD([sQuery(id+"F3.wireOp",EDGE,"E34.2.left")])]})]});
            var Q46;
            Q46=makeQuery(id+"F4.boolean.opBoolean","INTERSECT",EDGE,{"derivedFrom":[makeQuery(id+"F1.opExtrude","CAP_FACE",FACE,{"disambiguationData":[OSD([sQuery(id+"F0.wireOp",EDGE,"E0"),sQuery(id+"F0.wireOp",EDGE,"E2.MirrorCS"),sQuery(id+"F0.wireOp",EDGE,"E3"),sQuery(id+"F0.wireOp",EDGE,"E4.MirrorCS")])],"isStart":true}),makeQuery(id+"F4.opExtrude","SWEPT_FACE",FACE,{"disambiguationData":[OSD([sQuery(id+"F3.wireOp",EDGE,"E34.2.right")])]})]});
            var Q47;
            Q47=makeQuery(id+"F4.boolean.opBoolean","INTERSECT",EDGE,{"derivedFrom":[makeQuery(id+"F1.opExtrude","CAP_FACE",FACE,{"disambiguationData":[OSD([sQuery(id+"F0.wireOp",EDGE,"E0"),sQuery(id+"F0.wireOp",EDGE,"E2.MirrorCS"),sQuery(id+"F0.wireOp",EDGE,"E3"),sQuery(id+"F0.wireOp",EDGE,"E4.MirrorCS")])],"isStart":true}),makeQuery(id+"F4.opExtrude","SWEPT_FACE",FACE,{"disambiguationData":[OSD([sQuery(id+"F3.wireOp",EDGE,"E34.1.left")])]})]});
            var Q48;
            Q48=makeQuery(id+"F4.boolean.opBoolean","INTERSECT",EDGE,{"derivedFrom":[makeQuery(id+"F1.opExtrude","CAP_FACE",FACE,{"disambiguationData":[OSD([sQuery(id+"F0.wireOp",EDGE,"E0"),sQuery(id+"F0.wireOp",EDGE,"E2.MirrorCS"),sQuery(id+"F0.wireOp",EDGE,"E3"),sQuery(id+"F0.wireOp",EDGE,"E4.MirrorCS")])],"isStart":true}),makeQuery(id+"F4.opExtrude","SWEPT_FACE",FACE,{"disambiguationData":[OSD([sQuery(id+"F3.wireOp",EDGE,"E34.1.right")])]})]});
            var Q49;
            Q49=makeQuery(id+"F4.boolean.opBoolean","INTERSECT",EDGE,{"derivedFrom":[makeQuery(id+"F1.opExtrude","CAP_FACE",FACE,{"disambiguationData":[OSD([sQuery(id+"F0.wireOp",EDGE,"E0"),sQuery(id+"F0.wireOp",EDGE,"E2.MirrorCS"),sQuery(id+"F0.wireOp",EDGE,"E3"),sQuery(id+"F0.wireOp",EDGE,"E4.MirrorCS")])],"isStart":true}),makeQuery(id+"F4.opExtrude","SWEPT_FACE",FACE,{"disambiguationData":[OSD([sQuery(id+"F3.wireOp",EDGE,"E34.0.left")])]})]});
            var Q50;
            Q50=makeQuery(id+"F4.boolean.opBoolean","INTERSECT",EDGE,{"derivedFrom":[makeQuery(id+"F1.opExtrude","CAP_FACE",FACE,{"disambiguationData":[OSD([sQuery(id+"F0.wireOp",EDGE,"E0"),sQuery(id+"F0.wireOp",EDGE,"E2.MirrorCS"),sQuery(id+"F0.wireOp",EDGE,"E3"),sQuery(id+"F0.wireOp",EDGE,"E4.MirrorCS")])],"isStart":true}),makeQuery(id+"F4.opExtrude","SWEPT_FACE",FACE,{"disambiguationData":[OSD([sQuery(id+"F3.wireOp",EDGE,"E34.0.right")])]})]});
            var Q51;
            Q51=makeQuery(id+"F4.boolean.opBoolean","INTERSECT",EDGE,{"derivedFrom":[makeQuery(id+"F1.opExtrude","CAP_FACE",FACE,{"disambiguationData":[OSD([sQuery(id+"F0.wireOp",EDGE,"E0"),sQuery(id+"F0.wireOp",EDGE,"E2.MirrorCS"),sQuery(id+"F0.wireOp",EDGE,"E3"),sQuery(id+"F0.wireOp",EDGE,"E4.MirrorCS")])],"isStart":true}),makeQuery(id+"F4.opExtrude","SWEPT_FACE",FACE,{"disambiguationData":[OSD([sQuery(id+"F3.wireOp",EDGE,"E21.MirrorCS")])]})]});
            var Q52;
            Q52=makeQuery(id+"F4.boolean.opBoolean","INTERSECT",EDGE,{"derivedFrom":[makeQuery(id+"F1.opExtrude","CAP_FACE",FACE,{"disambiguationData":[OSD([sQuery(id+"F0.wireOp",EDGE,"E0"),sQuery(id+"F0.wireOp",EDGE,"E2.MirrorCS"),sQuery(id+"F0.wireOp",EDGE,"E3"),sQuery(id+"F0.wireOp",EDGE,"E4.MirrorCS")])],"isStart":true}),makeQuery(id+"F4.opExtrude","SWEPT_FACE",FACE,{"disambiguationData":[OSD([sQuery(id+"F3.wireOp",EDGE,"E27.MirrorCS")])]})]});
            var Q53;
            Q53=makeQuery(id+"F8.opExtrude","CAP_EDGE",EDGE,{"disambiguationData":[OSD([sQuery(id+"F7.wireOp",EDGE,"E60.0.right")])],"isStart":false});
            var Q54;
            Q54=makeQuery(id+"F8.opExtrude","CAP_EDGE",EDGE,{"disambiguationData":[OSD([sQuery(id+"F7.wireOp",EDGE,"E60.0.left")])],"isStart":false});
            fillet(context, id + "F9", {"entities" : qUnion([Q0, Q1, Q2, Q3, Q4, Q5, Q6, Q7, Q8, Q9, Q10, Q11, Q12, Q13, Q14, Q15, Q16, Q17, Q18, Q19, Q20, Q21, Q22, Q23, Q24, Q25, Q26, Q27, Q28, Q29, Q30, Q31, Q32, Q33, Q34, Q35, Q36, Q37, Q38, Q39, Q40, Q41, Q42, Q43, Q44, Q45, Q46, Q47, Q48, Q49, Q50, Q51, Q52, Q53, Q54]), "radius" : 1 * mm, "tangentPropagation" : true, "allowEdgeOverflow" : false});
        }
        {
            var Q0;
            Q0=makeQuery(id+"F4.boolean.opBoolean","COPY",EDGE,{"derivedFrom":makeQuery(id+"F4.opExtrude","CAP_EDGE",EDGE,{"disambiguationData":[OSD([sQuery(id+"F3.wireOp",EDGE,"E9.0.right")])],"isStart":true})});
            var Q1;
            Q1=makeQuery(id+"F4.boolean.opBoolean","COPY",EDGE,{"derivedFrom":makeQuery(id+"F4.opExtrude","CAP_EDGE",EDGE,{"disambiguationData":[OSD([sQuery(id+"F3.wireOp",EDGE,"E9.0.left")])],"isStart":true})});
            var Q2;
            Q2=makeQuery(id+"F4.boolean.opBoolean","COPY",EDGE,{"derivedFrom":makeQuery(id+"F4.opExtrude","CAP_EDGE",EDGE,{"disambiguationData":[OSD([sQuery(id+"F3.wireOp",EDGE,"E9.1.right")])],"isStart":true})});
            var Q3;
            Q3=makeQuery(id+"F4.boolean.opBoolean","COPY",EDGE,{"derivedFrom":makeQuery(id+"F4.opExtrude","CAP_EDGE",EDGE,{"disambiguationData":[OSD([sQuery(id+"F3.wireOp",EDGE,"E9.2.right")])],"isStart":true})});
            var Q4;
            Q4=makeQuery(id+"F4.boolean.opBoolean","COPY",EDGE,{"derivedFrom":makeQuery(id+"F4.opExtrude","CAP_EDGE",EDGE,{"disambiguationData":[OSD([sQuery(id+"F3.wireOp",EDGE,"E9.2.left")])],"isStart":true})});
            var Q5;
            Q5=makeQuery(id+"F4.boolean.opBoolean","COPY",EDGE,{"derivedFrom":makeQuery(id+"F4.opExtrude","CAP_EDGE",EDGE,{"disambiguationData":[OSD([sQuery(id+"F3.wireOp",EDGE,"E9.3.right")])],"isStart":true})});
            var Q6;
            Q6=makeQuery(id+"F4.boolean.opBoolean","COPY",EDGE,{"derivedFrom":makeQuery(id+"F4.opExtrude","CAP_EDGE",EDGE,{"disambiguationData":[OSD([sQuery(id+"F3.wireOp",EDGE,"E9.3.left")])],"isStart":true})});
            var Q7;
            Q7=makeQuery(id+"F4.boolean.opBoolean","COPY",EDGE,{"derivedFrom":makeQuery(id+"F4.opExtrude","CAP_EDGE",EDGE,{"disambiguationData":[OSD([sQuery(id+"F3.wireOp",EDGE,"E43.MirrorCS")])],"isStart":true})});
            var Q8;
            Q8=makeQuery(id+"F4.boolean.opBoolean","COPY",EDGE,{"derivedFrom":makeQuery(id+"F4.opExtrude","CAP_EDGE",EDGE,{"disambiguationData":[OSD([sQuery(id+"F3.wireOp",EDGE,"E48.MirrorCS")])],"isStart":true})});
            var Q9;
            Q9=makeQuery(id+"F4.boolean.opBoolean","COPY",EDGE,{"derivedFrom":makeQuery(id+"F4.opExtrude","CAP_EDGE",EDGE,{"disambiguationData":[OSD([sQuery(id+"F3.wireOp",EDGE,"E44.MirrorCS")])],"isStart":true})});
            var Q10;
            Q10=makeQuery(id+"F4.boolean.opBoolean","COPY",EDGE,{"derivedFrom":makeQuery(id+"F4.opExtrude","CAP_EDGE",EDGE,{"disambiguationData":[OSD([sQuery(id+"F3.wireOp",EDGE,"E42.MirrorCS")])],"isStart":true})});
            var Q11;
            Q11=makeQuery(id+"F4.boolean.opBoolean","COPY",EDGE,{"derivedFrom":makeQuery(id+"F4.opExtrude","CAP_EDGE",EDGE,{"disambiguationData":[OSD([sQuery(id+"F3.wireOp",EDGE,"E47.MirrorCS")])],"isStart":true})});
            var Q12;
            {var subQ0=makeQuery(id+"F4.opExtrude","SWEPT_FACE",FACE,{"disambiguationData":[OSD([sQuery(id+"F3.wireOp",EDGE,"E46.MirrorCS")])]});Q12=makeQuery(id+"F9.opFillet","BLEND_EDGE",EDGE,{"blendedFrom":[makeQuery(id+"F4.boolean.opBoolean","INTERSECT",EDGE,{"derivedFrom":[makeQuery(id+"F1.opExtrude","CAP_FACE",FACE,{"disambiguationData":[OSD([sQuery(id+"F0.wireOp",EDGE,"E0"),sQuery(id+"F0.wireOp",EDGE,"E2.MirrorCS"),sQuery(id+"F0.wireOp",EDGE,"E3"),sQuery(id+"F0.wireOp",EDGE,"E4.MirrorCS")])],"isStart":true}),subQ0]}),makeQuery(id+"F4.boolean.opBoolean","COPY",FACE,{"derivedFrom":subQ0})],"blendedInto":[makeQuery(id+"F4.boolean.opBoolean","COPY",FACE,{"derivedFrom":subQ0})]});}
            var Q13;
            Q13=makeQuery(id+"F4.boolean.opBoolean","COPY",EDGE,{"derivedFrom":makeQuery(id+"F4.opExtrude","CAP_EDGE",EDGE,{"disambiguationData":[OSD([sQuery(id+"F3.wireOp",EDGE,"E46.MirrorCS")])],"isStart":true})});
            var Q14;
            Q14=makeQuery(id+"F4.boolean.opBoolean","COPY",EDGE,{"derivedFrom":makeQuery(id+"F4.opExtrude","CAP_EDGE",EDGE,{"disambiguationData":[OSD([sQuery(id+"F3.wireOp",EDGE,"E18.MirrorCS")])],"isStart":true})});
            var Q15;
            Q15=makeQuery(id+"F4.boolean.opBoolean","COPY",EDGE,{"derivedFrom":makeQuery(id+"F4.opExtrude","CAP_EDGE",EDGE,{"disambiguationData":[OSD([sQuery(id+"F3.wireOp",EDGE,"E23.MirrorCS")])],"isStart":true})});
            var Q16;
            Q16=makeQuery(id+"F4.boolean.opBoolean","COPY",EDGE,{"derivedFrom":makeQuery(id+"F4.opExtrude","CAP_EDGE",EDGE,{"disambiguationData":[OSD([sQuery(id+"F3.wireOp",EDGE,"E19.MirrorCS")])],"isStart":true})});
            var Q17;
            Q17=makeQuery(id+"F4.boolean.opBoolean","COPY",EDGE,{"derivedFrom":makeQuery(id+"F4.opExtrude","CAP_EDGE",EDGE,{"disambiguationData":[OSD([sQuery(id+"F3.wireOp",EDGE,"E17.MirrorCS")])],"isStart":true})});
            var Q18;
            Q18=makeQuery(id+"F4.boolean.opBoolean","COPY",EDGE,{"derivedFrom":makeQuery(id+"F4.opExtrude","CAP_EDGE",EDGE,{"disambiguationData":[OSD([sQuery(id+"F3.wireOp",EDGE,"E29.MirrorCS")])],"isStart":true})});
            var Q19;
            Q19=makeQuery(id+"F4.boolean.opBoolean","COPY",EDGE,{"derivedFrom":makeQuery(id+"F4.opExtrude","CAP_EDGE",EDGE,{"disambiguationData":[OSD([sQuery(id+"F3.wireOp",EDGE,"E22.MirrorCS")])],"isStart":true})});
            var Q20;
            Q20=makeQuery(id+"F4.boolean.opBoolean","COPY",EDGE,{"derivedFrom":makeQuery(id+"F4.opExtrude","CAP_EDGE",EDGE,{"disambiguationData":[OSD([sQuery(id+"F3.wireOp",EDGE,"E27.MirrorCS")])],"isStart":true})});
            var Q21;
            Q21=makeQuery(id+"F4.boolean.opBoolean","COPY",EDGE,{"derivedFrom":makeQuery(id+"F4.opExtrude","CAP_EDGE",EDGE,{"disambiguationData":[OSD([sQuery(id+"F3.wireOp",EDGE,"E21.MirrorCS")])],"isStart":true})});
            var Q22;
            Q22=makeQuery(id+"F4.boolean.opBoolean","COPY",EDGE,{"derivedFrom":makeQuery(id+"F4.opExtrude","CAP_EDGE",EDGE,{"disambiguationData":[OSD([sQuery(id+"F3.wireOp",EDGE,"E34.3.left")])],"isStart":true})});
            var Q23;
            Q23=makeQuery(id+"F6.boolean.opBoolean","COPY",EDGE,{"derivedFrom":makeQuery(id+"F6.opExtrude","CAP_EDGE",EDGE,{"disambiguationData":[OSD([sQuery(id+"F5.wireOp",EDGE,"E55")])],"isStart":true})});
            var Q24;
            Q24=makeQuery(id+"F4.boolean.opBoolean","COPY",EDGE,{"derivedFrom":makeQuery(id+"F4.opExtrude","CAP_EDGE",EDGE,{"disambiguationData":[OSD([sQuery(id+"F3.wireOp",EDGE,"E34.2.right")])],"isStart":true})});
            var Q25;
            Q25=makeQuery(id+"F4.boolean.opBoolean","COPY",EDGE,{"derivedFrom":makeQuery(id+"F4.opExtrude","CAP_EDGE",EDGE,{"disambiguationData":[OSD([sQuery(id+"F3.wireOp",EDGE,"E34.1.right")])],"isStart":true})});
            var Q26;
            {var subQ0=makeQuery(id+"F4.opExtrude","SWEPT_FACE",FACE,{"disambiguationData":[OSD([sQuery(id+"F3.wireOp",EDGE,"E34.0.left")])]});Q26=makeQuery(id+"F9.opFillet","BLEND_EDGE",EDGE,{"blendedFrom":[makeQuery(id+"F4.boolean.opBoolean","INTERSECT",EDGE,{"derivedFrom":[makeQuery(id+"F1.opExtrude","CAP_FACE",FACE,{"disambiguationData":[OSD([sQuery(id+"F0.wireOp",EDGE,"E0"),sQuery(id+"F0.wireOp",EDGE,"E2.MirrorCS"),sQuery(id+"F0.wireOp",EDGE,"E3"),sQuery(id+"F0.wireOp",EDGE,"E4.MirrorCS")])],"isStart":true}),subQ0]}),makeQuery(id+"F4.boolean.opBoolean","COPY",FACE,{"derivedFrom":subQ0})],"blendedInto":[makeQuery(id+"F4.boolean.opBoolean","COPY",FACE,{"derivedFrom":subQ0})]});}
            var Q27;
            Q27=makeQuery(id+"F4.boolean.opBoolean","COPY",EDGE,{"derivedFrom":makeQuery(id+"F4.opExtrude","CAP_EDGE",EDGE,{"disambiguationData":[OSD([sQuery(id+"F3.wireOp",EDGE,"E34.0.left")])],"isStart":true})});
            fillet(context, id + "F10", {"entities" : qUnion([Q0, Q1, Q2, Q3, Q4, Q5, Q6, Q7, Q8, Q9, Q10, Q11, Q12, Q13, Q14, Q15, Q16, Q17, Q18, Q19, Q20, Q21, Q22, Q23, Q24, Q25, Q26, Q27]), "radius" : 1 * mm, "tangentPropagation" : true, "allowEdgeOverflow" : false});
        }
    });
